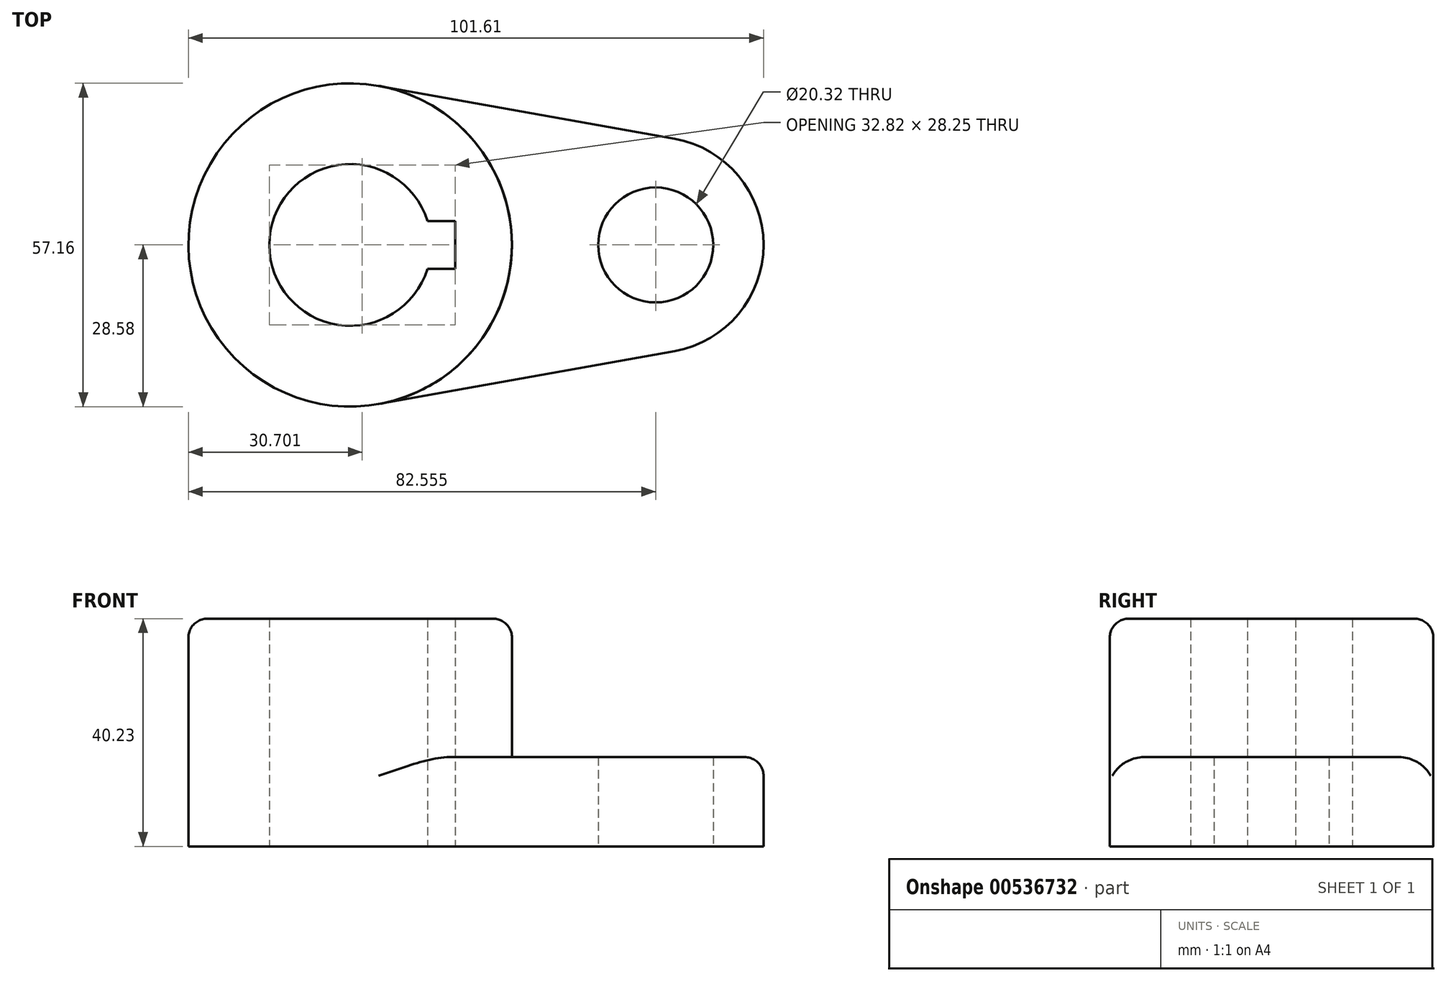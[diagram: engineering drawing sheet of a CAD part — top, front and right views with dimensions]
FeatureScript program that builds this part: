
annotation { "Feature Type Name" : "Feature", "Feature Type Description" : "" }
export const myFeature = defineFeature(function(context is Context, id is Id, definition is map)
    precondition{}
    {
        {
            var Q0;
            Q0=qCreatedBy(makeId("Top.planeOp"),FACE);
            var sketch = newSketch(context, id + "F0", { "sketchPlane" : qUnion([Q0])});
            skCircle(sketch, "E0", {"center": v(0, 0) * mm, "radius": 28.58 * mm});
            skArc(sketch, "E1", {"start": v(57.34, -18.75) * mm, "mid": v(73.03, 0) * mm, "end": v(57.34, 18.75) * mm});
            skLineSegment(sketch, "E2", {"start": v(0, 0) * mm, "end": v(53.98, 0) * mm, "construction": true});
            skLineSegment(sketch, "E3", {"start": v(5.04, 28.13) * mm, "end": v(57.34, 18.75) * mm});
            skLineSegment(sketch, "E4", {"start": v(5.04, -28.13) * mm, "end": v(57.34, -18.75) * mm});
            skCircle(sketch, "E5", {"center": v(0, 0) * mm, "radius": 14.29 * mm});
            skCircle(sketch, "E6", {"center": v(53.98, 0) * mm, "radius": 10.16 * mm});
            skLineSegment(sketch, "E7", {"start": v(-14.29, 0) * mm, "end": v(18.53, 0) * mm});
            skLineSegment(sketch, "E8.bottom", {"start": v(18.53, 4.24) * mm, "end": v(10.05, 4.24) * mm});
            skLineSegment(sketch, "E8.top", {"start": v(18.53, -4.24) * mm, "end": v(10.05, -4.24) * mm});
            skLineSegment(sketch, "E8.left", {"start": v(18.53, 4.24) * mm, "end": v(18.53, -4.24) * mm});
            skLineSegment(sketch, "E8.right", {"start": v(10.05, 4.24) * mm, "end": v(10.05, -4.24) * mm});
            skPoint(sketch, "E8.middle", {"position": v(14.29, 0) * mm});
            skSolve(sketch);
        }
        {
            var Q0;
            Q0=makeQuery(id+"F0.imprint","IMPRINT",FACE,{"disambiguationData":[TD([[makeQuery(id+"F0.imprint","IMPRINT",EDGE,{"derivedFrom":sQuery(id+"F0.wireOp",EDGE,"E1")}),1.0]])]});
            extrude(context, id + "F1", {"entities" : qUnion([Q0]), "depth" : 15.77 * mm, "offsetDistance" : 25.4 * mm});
        }
        {
            var Q0;
            Q0=makeQuery(id+"F0.imprint","IMPRINT",FACE,{"disambiguationData":[TD([[makeQuery(id+"F0.imprint","IMPRINT",EDGE,{"derivedFrom":sQuery(id+"F0.wireOp",EDGE,"E5")}),-1.0]])]});
            extrude(context, id + "F2", {"entities" : qUnion([Q0]), "operationType" : NewBodyOperationType.ADD, "depth" : 40.23 * mm, "offsetDistance" : 25.4 * mm});
        }
        {
            var Q0;
            Q0=qCreatedBy(makeId("Right.planeOp"),FACE);
            var sketch = newSketch(context, id + "F3", { "sketchPlane" : qUnion([Q0])});
            skLineSegment(sketch, "E9", {"start": v(-28.58, 0) * mm, "end": v(-28.58, 39.75) * mm});
            skLineSegment(sketch, "E10", {"start": v(28.58, 40.23) * mm, "end": v(28.58, 0) * mm});
            skLineSegment(sketch, "E11", {"start": v(-28.58, 0) * mm, "end": v(-28.58, 40.23) * mm});
            skLineSegment(sketch, "E12.0", {"start": v(-28.58, 40.23) * mm, "end": v(28.58, 40.23) * mm});
            skLineSegment(sketch, "E13.left", {"start": v(-28.58, 39.75) * mm, "end": v(-28.58, 36.45) * mm});
            skLineSegment(sketch, "E14", {"start": v(-25.27, 36.93) * mm, "end": v(-25.27, 40.23) * mm});
            skArc(sketch, "E15", {"start": v(-25.27, 40.23) * mm, "mid": v(-27.6, 39.27) * mm, "end": v(-28.58, 36.93) * mm});
            skLineSegment(sketch, "E16", {"start": v(-28.58, 36.93) * mm, "end": v(-25.27, 36.93) * mm});
            skLineSegment(sketch, "E17", {"start": v(-28.58, 36.93) * mm, "end": v(-28.58, 40.23) * mm});
            skLineSegment(sketch, "E18", {"start": v(-25.27, 40.23) * mm, "end": v(-28.58, 40.23) * mm});
            skLineSegment(sketch, "E19", {"start": v(0, 0) * mm, "end": v(0, 42.75) * mm});
            skPoint(sketch, "E19.endSnap0", {"position": v(0, 40.23) * mm});
            skSolve(sketch);
        }
        {
            var Q0;
            {var subQ0=sQuery(id+"F3.wireOp",EDGE,"E15");Q0=makeQuery(id+"F3.imprint","IMPRINT",FACE,{"disambiguationData":[TD([[makeQuery(id+"F3.imprint","IMPRINT",EDGE,{"derivedFrom":subQ0}),-1.0]])]});}
            var Q1;
            Q1=sQuery(id+"F3.wireOp",EDGE,"E19");
            revolve(context, id + "F4", {"operationType" : NewBodyOperationType.REMOVE, "entities" : qUnion([Q0]), "axis" : qUnion([Q1]), "revolveType" : RevolveType.FULL, "oppositeDirection" : true});
        }
        {
            var Q0;
            Q0=makeQuery(id+"F1.opExtrude","CAP_EDGE",EDGE,{"disambiguationData":[OSD([sQuery(id+"F0.wireOp",EDGE,"E4")])],"isStart":false});
            fillet(context, id + "F5", {"entities" : qUnion([Q0]), "radius" : 3.3 * mm, "tangentPropagation" : true, "allowEdgeOverflow" : false});
        }
    });
